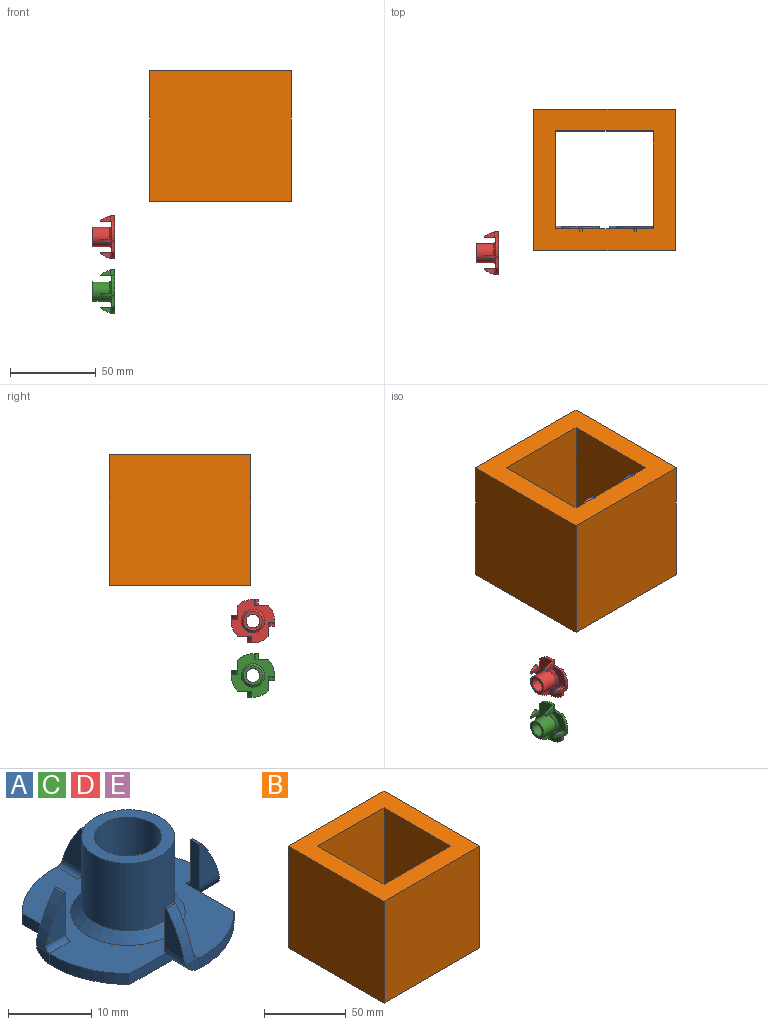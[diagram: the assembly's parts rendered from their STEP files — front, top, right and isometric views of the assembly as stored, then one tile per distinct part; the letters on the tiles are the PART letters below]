
ASSEMBLY  parts=5 mates=2
PART A: 47 faces, bbox 25.4x25.4x12.7 mm
  f0: cylinder r=12.7mm len=9.78mm, axis (0,0,-1), area 17.1mm2, adj f9,f12,f36,f38
  f1: cylinder r=16.73mm len=6.81mm, axis (0,-1,0), area 12mm2, adj f2,f3,f4,f5,f6,f7
  f2: plane 2.21x1.58mm, normal (1,0,0), area 2.5mm2, adj f1,f7,f37
  f3: cylinder r=0.76mm len=3.54mm, axis (-1,0,0), area 4.2mm2, adj f1,f4,f8,f38
  f4: plane 6.05x3.36mm, normal (0,1,0), area 12.7mm2, adj f1,f3,f5,f8
  f5: plane 1.58x0.34mm, normal (0,0,1), area 0.5mm2, adj f1,f4,f6,f8
  f6: plane 6.05x3.36mm, normal (0,-1,0), area 12.7mm2, adj f1,f5,f7,f8
  f7: cylinder r=2.34mm len=3.54mm, axis (-1,0,0), area 12.9mm2, adj f1,f2,f6,f8,f9,f36
  f8: plane 6.81x2.34mm, normal (-1,0,0), area 10.8mm2, adj f3,f4,f5,f6,f7,f38
  f9: plane 8.18x1.58mm, normal (1,0,0), area 10.3mm2, adj f0,f7,f36,f38
  f10: cylinder r=12.7mm len=9.78mm, axis (0,0,-1), area 17.1mm2, adj f19,f22,f36,f38
  f11: cylinder r=16.73mm len=6.81mm, axis (-1,0,0), area 12mm2, adj f12,f13,f14,f15,f16,f17
  f12: plane 2.21x1.58mm, normal (0,-1,0), area 2.5mm2, adj f0,f11,f17
  f13: cylinder r=0.76mm len=3.54mm, axis (0,1,0), area 4.2mm2, adj f11,f14,f18,f38
  f14: plane 6.05x3.36mm, normal (1,0,0), area 12.7mm2, adj f11,f13,f15,f18
  f15: plane 1.58x0.34mm, normal (0,0,1), area 0.5mm2, adj f11,f14,f16,f18
  f16: plane 6.05x3.36mm, normal (-1,0,0), area 12.7mm2, adj f11,f15,f17,f18
  f17: cylinder r=2.34mm len=3.54mm, axis (0,1,0), area 12.9mm2, adj f11,f12,f16,f18,f19,f36
  f18: plane 6.81x2.34mm, normal (0,1,0), area 10.8mm2, adj f13,f14,f15,f16,f17,f38
  f19: plane 8.18x1.58mm, normal (0,-1,0), area 10.3mm2, adj f10,f17,f36,f38
  f20: cylinder r=12.7mm len=9.78mm, axis (0,0,-1), area 17.1mm2, adj f29,f30,f36,f38
  f21: cylinder r=16.73mm len=6.81mm, axis (0,1,0), area 12mm2, adj f22,f23,f24,f25,f26,f27
  f22: plane 2.21x1.58mm, normal (-1,0,0), area 2.5mm2, adj f10,f21,f27
  f23: cylinder r=0.76mm len=3.54mm, axis (1,0,0), area 4.2mm2, adj f21,f24,f28,f38
  f24: plane 6.05x3.36mm, normal (0,-1,0), area 12.7mm2, adj f21,f23,f25,f28
  f25: plane 1.58x0.34mm, normal (0,0,1), area 0.5mm2, adj f21,f24,f26,f28
  f26: plane 6.05x3.36mm, normal (0,1,0), area 12.7mm2, adj f21,f25,f27,f28
  f27: cylinder r=2.34mm len=3.54mm, axis (1,0,0), area 12.9mm2, adj f21,f22,f26,f28,f29,f36
  f28: plane 6.81x2.34mm, normal (1,0,0), area 10.8mm2, adj f23,f24,f25,f26,f27,f38
  f29: plane 8.18x1.58mm, normal (-1,0,0), area 10.3mm2, adj f20,f27,f36,f38
  f30: plane 2.21x1.58mm, normal (0,1,0), area 2.5mm2, adj f20,f34,f46
  f31: cylinder r=0.76mm len=3.54mm, axis (0,-1,0), area 4.2mm2, adj f32,f38,f45,f46
  f32: plane 6.05x3.36mm, normal (-1,0,0), area 12.7mm2, adj f31,f33,f45,f46
  f33: plane 1.58x0.34mm, normal (0,0,1), area 0.5mm2, adj f32,f44,f45,f46
  f34: cylinder r=2.34mm len=3.54mm, axis (0,-1,0), area 12.9mm2, adj f30,f36,f43,f44,f45,f46
  f35: cone r=4.01mm half-angle=45deg, axis (0,0,-1), area 99.5mm2, adj f36,f42
  f36: plane 25.4x25.4mm, normal (0,0,-1), area 308.5mm2, adj f0,f7,f9,f10,f17,f19,f20,f27
  f37: cylinder r=12.7mm len=9.78mm, axis (0,0,-1), area 17.1mm2, adj f2,f36,f38,f43
  f38: plane 25.4x25.4mm, normal (0,0,1), area 281.7mm2, adj f0,f3,f8,f9,f10,f13,f18,f19
  f39: cone r=6.86mm half-angle=45deg, axis (0,0,-1), area 70.2mm2, adj f38,f40
  f40: cylinder r=5.59mm len=11.18mm, axis (0,0,-1), area 346mm2, adj f39,f41
  f41: plane 11.18x11.18mm, normal (0,0,1), area 47.5mm2, adj f40,f42
  f42: cylinder r=4.01mm len=10.51mm, axis (0,0,-1), area 265mm2, adj f35,f41
  f43: plane 8.18x1.58mm, normal (0,1,0), area 10.3mm2, adj f34,f36,f37,f38
  f44: plane 6.05x3.36mm, normal (1,0,0), area 12.7mm2, adj f33,f34,f45,f46
  f45: plane 6.81x2.34mm, normal (0,-1,0), area 10.8mm2, adj f31,f32,f33,f34,f38,f44
  f46: cylinder r=16.73mm len=6.81mm, axis (1,0,0), area 12mm2, adj f30,f31,f32,f33,f34,f44
PART B: 10 faces, bbox 82.6x82.6x76.2 mm
  f0: plane 76.2x57.15mm, normal (0,1,0), area 4354.8mm2, adj f1,f7,f8,f9
  f1: plane 76.2x57.15mm, normal (1,0,0), area 4354.8mm2, adj f0,f2,f8,f9
  f2: plane 76.2x57.15mm, normal (0,-1,0), area 4354.8mm2, adj f1,f7,f8,f9
  f3: plane 82.55x76.2mm, normal (-1,0,0), area 6290.3mm2, adj f4,f6,f8,f9
  f4: plane 82.55x76.2mm, normal (0,-1,0), area 6290.3mm2, adj f3,f5,f8,f9
  f5: plane 82.55x76.2mm, normal (1,0,0), area 6290.3mm2, adj f4,f6,f8,f9
  f6: plane 82.55x76.2mm, normal (0,1,0), area 6290.3mm2, adj f3,f5,f8,f9
  f7: plane 76.2x57.15mm, normal (-1,0,0), area 4354.8mm2, adj f0,f2,f8,f9
  f8: plane 82.55x82.55mm, normal (0,0,1), area 3548.4mm2, adj f0,f1,f2,f3,f4,f5,f6,f7
  f9: plane 82.55x82.55mm, normal (0,0,-1), area 3548.4mm2, adj f0,f1,f2,f3,f4,f5,f6,f7
PART C: same geometry as A
PART D: same geometry as A
PART E: same geometry as A
PLACE A rot(axis=(1,0,0),90deg) t=(63.93,16.47,67.9)mm
PLACE B t=(6.78,2.19,4.4)mm
PLACE C rot(axis=(0,-1,0),90deg) t=(-13.75,0.95,-48.14)mm
PLACE D rot(axis=(0,-1,0),90deg) t=(-13.75,0.95,-16.39)mm
PLACE E rot(axis=(1,0,0),90deg) t=(32.18,16.47,67.9)mm
MATE fastened A.f0 <-> B.f0  axis (0,-1,0) through (63.93,14.89,67.9)mm
MATE fastened E.f0 <-> B.f0  axis (0,-1,0) through (32.18,14.89,67.9)mm
